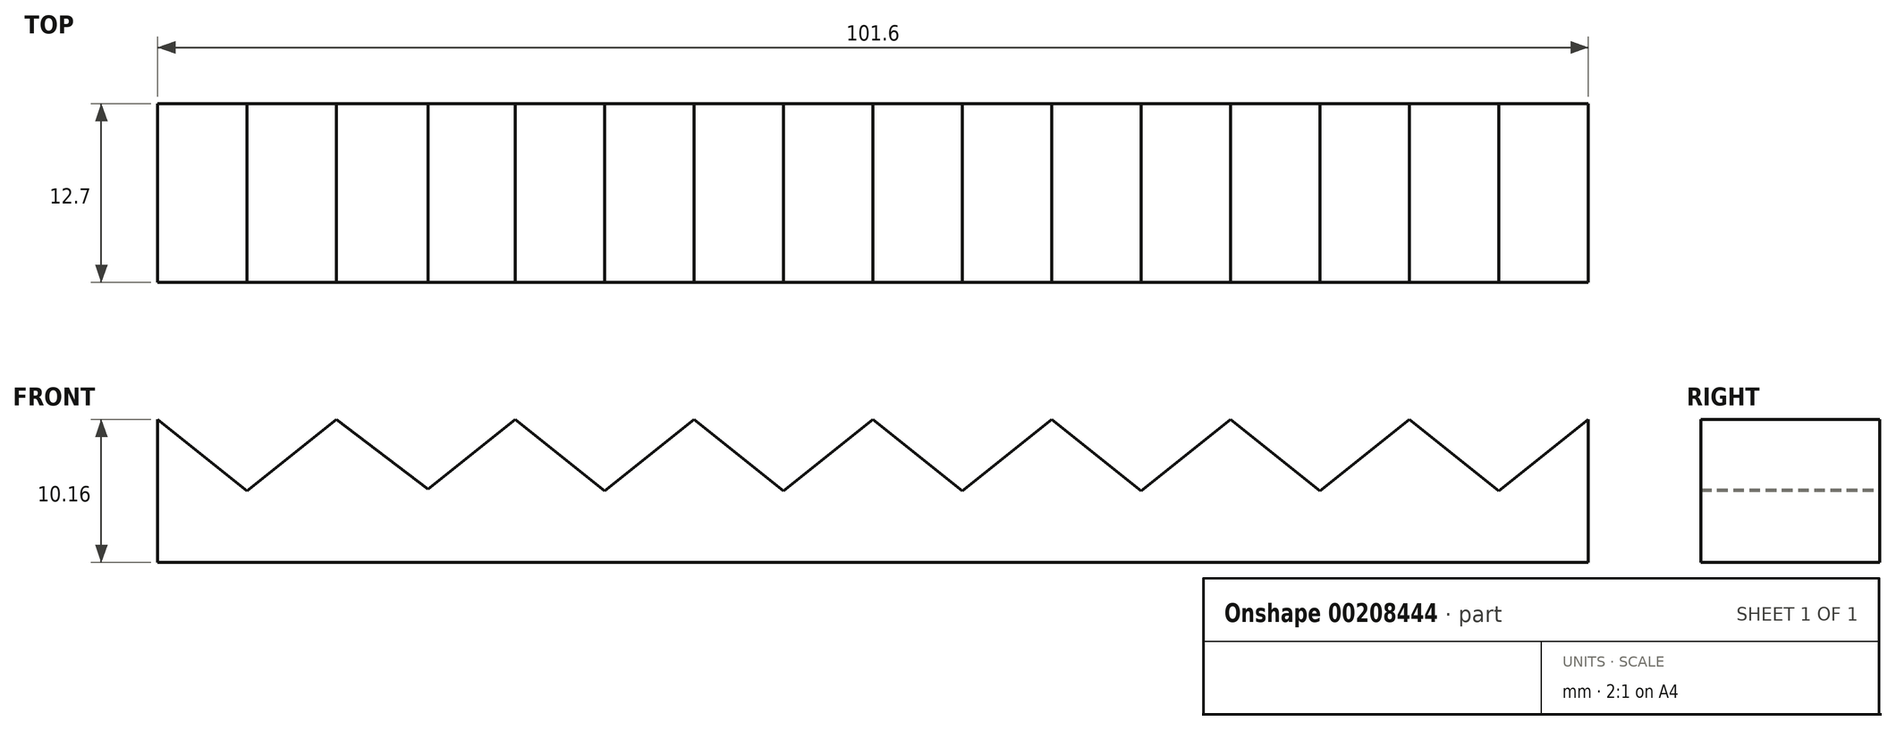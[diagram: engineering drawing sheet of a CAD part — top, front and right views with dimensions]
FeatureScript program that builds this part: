
annotation { "Feature Type Name" : "Feature", "Feature Type Description" : "" }
export const myFeature = defineFeature(function(context is Context, id is Id, definition is map)
    precondition{}
    {
        {
            var Q0;
            Q0=qCreatedBy(makeId("Front.planeOp"),FACE);
            var sketch = newSketch(context, id + "F0", { "sketchPlane" : qUnion([Q0])});
            skLineSegment(sketch, "E0.top", {"start": v(25.4, -2.54) * mm, "end": v(-25.4, -2.54) * mm});
            skLineSegment(sketch, "E0.left", {"start": v(25.4, 2.54) * mm, "end": v(25.4, -2.54) * mm});
            skLineSegment(sketch, "E0.right", {"start": v(-25.4, 2.54) * mm, "end": v(-25.4, -2.54) * mm});
            skPoint(sketch, "E0.middle", {"position": v(0, 0) * mm});
            skLineSegment(sketch, "E1", {"start": v(-25.4, -2.54) * mm, "end": v(0, -2.54) * mm});
            skLineSegment(sketch, "E2", {"start": v(-12.7, -2.54) * mm, "end": v(-19.05, -2.54) * mm});
            skLineSegment(sketch, "E3", {"start": v(-12.7, -2.54) * mm, "end": v(-6.35, -2.54) * mm});
            skLineSegment(sketch, "E4", {"start": v(0, -2.54) * mm, "end": v(12.7, -2.54) * mm});
            skLineSegment(sketch, "E5", {"start": v(12.7, -2.54) * mm, "end": v(19.05, -2.54) * mm});
            skLineSegment(sketch, "E6", {"start": v(19.05, -2.54) * mm, "end": v(6.35, -2.54) * mm});
            skLineSegment(sketch, "E7", {"start": v(-25.4, 2.54) * mm, "end": v(-22.23, 0) * mm});
            skLineSegment(sketch, "E8", {"start": v(-15.8, 0.06) * mm, "end": v(-12.7, 2.54) * mm});
            skLineSegment(sketch, "E9", {"start": v(-12.7, 2.54) * mm, "end": v(-9.53, 0) * mm});
            skLineSegment(sketch, "E10", {"start": v(-3.18, 0) * mm, "end": v(0, 2.54) * mm});
            skLineSegment(sketch, "E11", {"start": v(0, 2.54) * mm, "end": v(3.18, 0) * mm});
            skLineSegment(sketch, "E12", {"start": v(9.53, 0) * mm, "end": v(12.7, 2.54) * mm});
            skLineSegment(sketch, "E13", {"start": v(12.7, 2.54) * mm, "end": v(15.88, 0) * mm});
            skLineSegment(sketch, "E14", {"start": v(22.23, 0) * mm, "end": v(25.4, 2.54) * mm});
            skLineSegment(sketch, "E15", {"start": v(22.23, 0) * mm, "end": v(19.05, 2.54) * mm});
            skLineSegment(sketch, "E16", {"start": v(19.05, 2.54) * mm, "end": v(15.88, 0) * mm});
            skLineSegment(sketch, "E17", {"start": v(9.53, 0) * mm, "end": v(6.35, 2.54) * mm});
            skLineSegment(sketch, "E18", {"start": v(6.35, 2.54) * mm, "end": v(3.18, 0) * mm});
            skLineSegment(sketch, "E19", {"start": v(-3.18, 0) * mm, "end": v(-6.35, 2.54) * mm});
            skLineSegment(sketch, "E20", {"start": v(-6.35, 2.54) * mm, "end": v(-9.53, 0) * mm});
            skLineSegment(sketch, "E21", {"start": v(-15.8, 0.06) * mm, "end": v(-19.05, 2.54) * mm});
            skLineSegment(sketch, "E22", {"start": v(-19.05, 2.54) * mm, "end": v(-22.23, 0) * mm});
            skSolve(sketch);
        }
        {
            var Q0;
            Q0=makeQuery(id+"F0.imprint","IMPRINT",FACE,{"disambiguationData":[TD([[makeQuery(id+"F0.imprint","IMPRINT",EDGE,{"derivedFrom":sQuery(id+"F0.wireOp",EDGE,"E0.top")}),-1.0]])]});
            extrude(context, id + "F1", {"entities" : qUnion([Q0]), "depth" : 6.35 * mm});
        }
        {
            var Q0;
            Q0=makeQuery(id+"F1.opExtrude","SWEPT_BODY",BODY,{"disambiguationData":[OSD([sQuery(id+"F0.wireOp",EDGE,"E0.top"),sQuery(id+"F0.wireOp",EDGE,"E0.left"),sQuery(id+"F0.wireOp",EDGE,"E0.right"),sQuery(id+"F0.wireOp",EDGE,"E1"),sQuery(id+"F0.wireOp",EDGE,"E2"),sQuery(id+"F0.wireOp",EDGE,"E3"),sQuery(id+"F0.wireOp",EDGE,"E4"),sQuery(id+"F0.wireOp",EDGE,"E6"),sQuery(id+"F0.wireOp",EDGE,"E7"),sQuery(id+"F0.wireOp",EDGE,"E8"),sQuery(id+"F0.wireOp",EDGE,"E9"),sQuery(id+"F0.wireOp",EDGE,"E10"),sQuery(id+"F0.wireOp",EDGE,"E11"),sQuery(id+"F0.wireOp",EDGE,"E12"),sQuery(id+"F0.wireOp",EDGE,"E13"),sQuery(id+"F0.wireOp",EDGE,"E14"),sQuery(id+"F0.wireOp",EDGE,"E15"),sQuery(id+"F0.wireOp",EDGE,"E16"),sQuery(id+"F0.wireOp",EDGE,"E17"),sQuery(id+"F0.wireOp",EDGE,"E18"),sQuery(id+"F0.wireOp",EDGE,"E19"),sQuery(id+"F0.wireOp",EDGE,"E20"),sQuery(id+"F0.wireOp",EDGE,"E21"),sQuery(id+"F0.wireOp",EDGE,"E22")])]});
            var Q1;
            Q1=qCreatedBy(makeId("Origin.pointOp"),VERTEX);
            transform(context, id + "F2", {"entities" : qUnion([Q0]), "transformType" : TransformType.SCALE_UNIFORMLY, "scale" : 2, "scalePoint" : qUnion([Q1]), "makeCopy" : false});
        }
    });
